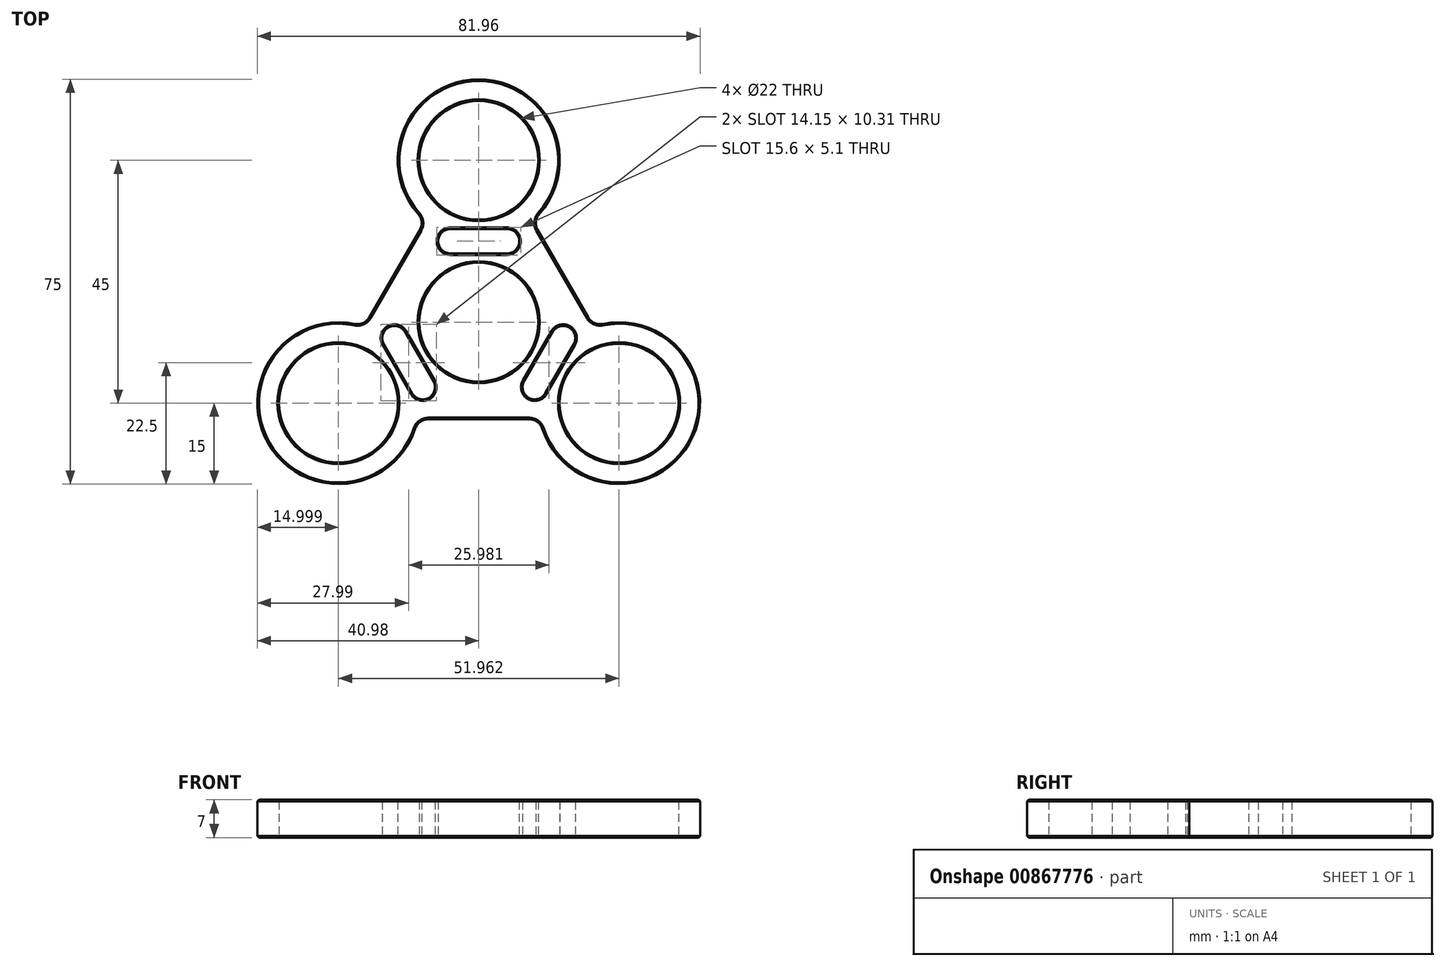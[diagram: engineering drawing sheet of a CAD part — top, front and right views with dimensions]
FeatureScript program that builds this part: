
annotation { "Feature Type Name" : "Feature", "Feature Type Description" : "" }
export const myFeature = defineFeature(function(context is Context, id is Id, definition is map)
    precondition{}
    {
        {
            var Q0;
            Q0=qCreatedBy(makeId("Top.planeOp"),FACE);
            var sketch = newSketch(context, id + "F0", { "sketchPlane" : qUnion([Q0])});
            skCircle(sketch, "E0", {"center": v(0, 0) * mm, "radius": 11 * mm});
            skCircle(sketch, "E1.cCircle", {"center": v(0, 0) * mm, "radius": 30 * mm, "construction": true});
            skLineSegment(sketch, "E1.0", {"start": v(0, 30) * mm, "end": v(25.98, -15) * mm, "construction": true});
            skLineSegment(sketch, "E1.1", {"start": v(25.98, -15) * mm, "end": v(-25.98, -15) * mm, "construction": true});
            skLineSegment(sketch, "E1.2", {"start": v(-25.98, -15) * mm, "end": v(0, 30) * mm, "construction": true});
            skCircle(sketch, "E2", {"center": v(0, 30) * mm, "radius": 11 * mm});
            skCircle(sketch, "E3.1.0", {"center": v(-25.98, -15) * mm, "radius": 11 * mm});
            skCircle(sketch, "E3.2.0", {"center": v(25.98, -15) * mm, "radius": 11 * mm});
            skArc(sketch, "E4", {"start": v(9.95, 18.77) * mm, "mid": v(0, 45) * mm, "end": v(-9.95, 18.77) * mm});
            skArc(sketch, "E5.1.0", {"start": v(-21.23, -0.77) * mm, "mid": v(-38.97, -22.5) * mm, "end": v(-11.28, -18) * mm});
            skArc(sketch, "E5.2.0", {"start": v(11.28, -18) * mm, "mid": v(38.97, -22.5) * mm, "end": v(21.23, -0.77) * mm});
            skLineSegment(sketch, "E6.2", {"start": v(11.28, -18) * mm, "end": v(-11.28, -18) * mm});
            skLineSegment(sketch, "E7.trimOffspring", {"start": v(-21.23, -0.77) * mm, "end": v(-9.95, 18.77) * mm});
            skLineSegment(sketch, "E8.trimOffspring", {"start": v(9.95, 18.77) * mm, "end": v(21.23, -0.77) * mm});
            skCircle(sketch, "E9", {"center": v(0, 0) * mm, "radius": 45 * mm, "construction": true});
            skSolve(sketch);
        }
        {
            var Q0;
            Q0=makeQuery(id+"F0.imprint","IMPRINT",FACE,{"disambiguationData":[TD([[makeQuery(id+"F0.imprint","IMPRINT",EDGE,{"derivedFrom":sQuery(id+"F0.wireOp",EDGE,"E0")}),-1.0]])]});
            extrude(context, id + "F1", {"entities" : qUnion([Q0]), "depth" : 7 * mm, "offsetDistance" : 25 * mm});
        }
        {
            var Q0;
            Q0=makeQuery(id+"F1.opExtrude","SWEPT_EDGE",EDGE,{"disambiguationData":[OSD([sQuery(id+"F0.wireOp",EDGE,"E5.2.0"),sQuery(id+"F0.wireOp",EDGE,"E6.2")])]});
            var Q1;
            Q1=makeQuery(id+"F1.opExtrude","SWEPT_EDGE",EDGE,{"disambiguationData":[OSD([sQuery(id+"F0.wireOp",EDGE,"E5.1.0"),sQuery(id+"F0.wireOp",EDGE,"E6.2")])]});
            var Q2;
            Q2=makeQuery(id+"F1.opExtrude","SWEPT_EDGE",EDGE,{"disambiguationData":[OSD([sQuery(id+"F0.wireOp",EDGE,"E5.1.0"),sQuery(id+"F0.wireOp",EDGE,"E7.trimOffspring")])]});
            var Q3;
            Q3=makeQuery(id+"F1.opExtrude","SWEPT_EDGE",EDGE,{"disambiguationData":[OSD([sQuery(id+"F0.wireOp",EDGE,"E4"),sQuery(id+"F0.wireOp",EDGE,"E8.trimOffspring")])]});
            var Q4;
            Q4=makeQuery(id+"F1.opExtrude","SWEPT_EDGE",EDGE,{"disambiguationData":[OSD([sQuery(id+"F0.wireOp",EDGE,"E5.2.0"),sQuery(id+"F0.wireOp",EDGE,"E8.trimOffspring")])]});
            var Q5;
            Q5=makeQuery(id+"F1.opExtrude","SWEPT_EDGE",EDGE,{"disambiguationData":[OSD([sQuery(id+"F0.wireOp",EDGE,"E4"),sQuery(id+"F0.wireOp",EDGE,"E7.trimOffspring")])]});
            fillet(context, id + "F2", {"entities" : qUnion([Q0, Q1, Q2, Q3, Q4, Q5]), "radius" : 2.5 * mm, "tangentPropagation" : true, "allowEdgeOverflow" : false});
        }
        {
            var Q0;
            Q0=makeQuery(id+"F1.opExtrude","CAP_FACE",FACE,{"disambiguationData":[OSD([sQuery(id+"F0.wireOp",EDGE,"E0"),sQuery(id+"F0.wireOp",EDGE,"E2"),sQuery(id+"F0.wireOp",EDGE,"E3.1.0"),sQuery(id+"F0.wireOp",EDGE,"E3.2.0"),sQuery(id+"F0.wireOp",EDGE,"E4"),sQuery(id+"F0.wireOp",EDGE,"E5.1.0"),sQuery(id+"F0.wireOp",EDGE,"E5.2.0"),sQuery(id+"F0.wireOp",EDGE,"E6.2"),sQuery(id+"F0.wireOp",EDGE,"E7.trimOffspring"),sQuery(id+"F0.wireOp",EDGE,"E8.trimOffspring")])],"isStart":true});
            var sketch = newSketch(context, id + "F3", { "sketchPlane" : qUnion([Q0])});
            skLineSegment(sketch, "E10.bottom", {"start": v(5.25, -12.75) * mm, "end": v(-5.25, -12.75) * mm});
            skLineSegment(sketch, "E10.top", {"start": v(5.25, -17.25) * mm, "end": v(-5.25, -17.25) * mm});
            skLineSegment(sketch, "E10.left", {"start": v(7.5, -15) * mm, "end": v(7.5, -15) * mm});
            skLineSegment(sketch, "E10.right", {"start": v(-7.5, -15) * mm, "end": v(-7.5, -15) * mm});
            skPoint(sketch, "E10.middle", {"position": v(0, -15) * mm});
            skPoint(sketch, "E11.center", {"position": v(0, 0) * mm});
            skPoint(sketch, "E12.visualSharp", {"position": v(7.5, -17.25) * mm});
            skArc(sketch, "E12.filletArc", {"start": v(5.25, -17.25) * mm, "mid": v(6.84, -16.6) * mm, "end": v(7.5, -15) * mm});
            skPoint(sketch, "E13.visualSharp", {"position": v(7.5, -12.75) * mm});
            skArc(sketch, "E13.filletArc", {"start": v(7.5, -15) * mm, "mid": v(6.84, -13.4) * mm, "end": v(5.25, -12.75) * mm});
            skPoint(sketch, "E14.visualSharp", {"position": v(-7.5, -17.25) * mm});
            skArc(sketch, "E14.filletArc", {"start": v(-7.5, -15) * mm, "mid": v(-6.84, -16.6) * mm, "end": v(-5.25, -17.25) * mm});
            skPoint(sketch, "E15.visualSharp", {"position": v(-7.5, -12.75) * mm});
            skArc(sketch, "E15.filletArc", {"start": v(-5.25, -12.75) * mm, "mid": v(-6.84, -13.4) * mm, "end": v(-7.5, -15) * mm});
            skPoint(sketch, "E16.1.0", {"position": v(13, 7.5) * mm});
            skArc(sketch, "E16.1.1", {"start": v(16.74, 1) * mm, "mid": v(17.79, 2.37) * mm, "end": v(17.56, 4.08) * mm});
            skPoint(sketch, "E16.1.2", {"position": v(14.8, -0.12) * mm});
            skLineSegment(sketch, "E16.1.3", {"start": v(12.31, 13.17) * mm, "end": v(17.56, 4.08) * mm});
            skArc(sketch, "E16.1.4", {"start": v(13.67, 1.83) * mm, "mid": v(15.03, 0.78) * mm, "end": v(16.74, 1) * mm});
            skPoint(sketch, "E16.1.5", {"position": v(11.19, 15.12) * mm});
            skPoint(sketch, "E16.1.6", {"position": v(7.3, 12.87) * mm});
            skPoint(sketch, "E16.1.7", {"position": v(18.69, 2.13) * mm});
            skLineSegment(sketch, "E16.1.8", {"start": v(8.42, 10.92) * mm, "end": v(13.67, 1.83) * mm});
            skArc(sketch, "E16.1.9", {"start": v(12.31, 13.17) * mm, "mid": v(10.95, 14.22) * mm, "end": v(9.24, 14) * mm});
            skArc(sketch, "E16.1.10", {"start": v(9.24, 14) * mm, "mid": v(8.2, 12.63) * mm, "end": v(8.42, 10.92) * mm});
            skPoint(sketch, "E16.2.0", {"position": v(-13, 7.5) * mm});
            skArc(sketch, "E16.2.1", {"start": v(-9.24, 14) * mm, "mid": v(-10.95, 14.22) * mm, "end": v(-12.31, 13.17) * mm});
            skPoint(sketch, "E16.2.2", {"position": v(-7.3, 12.87) * mm});
            skLineSegment(sketch, "E16.2.3", {"start": v(-17.56, 4.08) * mm, "end": v(-12.31, 13.17) * mm});
            skArc(sketch, "E16.2.4", {"start": v(-8.42, 10.92) * mm, "mid": v(-8.2, 12.63) * mm, "end": v(-9.24, 14) * mm});
            skPoint(sketch, "E16.2.5", {"position": v(-18.69, 2.13) * mm});
            skPoint(sketch, "E16.2.6", {"position": v(-14.8, -0.12) * mm});
            skPoint(sketch, "E16.2.7", {"position": v(-11.19, 15.12) * mm});
            skLineSegment(sketch, "E16.2.8", {"start": v(-13.67, 1.83) * mm, "end": v(-8.42, 10.92) * mm});
            skArc(sketch, "E16.2.9", {"start": v(-17.56, 4.08) * mm, "mid": v(-17.79, 2.37) * mm, "end": v(-16.74, 1) * mm});
            skArc(sketch, "E16.2.10", {"start": v(-16.74, 1) * mm, "mid": v(-15.03, 0.78) * mm, "end": v(-13.67, 1.83) * mm});
            skSolve(sketch);
        }
        {
            var Q0;
            Q0 = qSketchRegion(id + "F3", true);
            extrude(context, id + "F4", {"entities" : qUnion([Q0]), "operationType" : NewBodyOperationType.REMOVE, "oppositeDirection" : true, "depth" : 25 * mm, "offsetDistance" : 25 * mm});
        }
        {
            var Q0;
            Q0=makeQuery(id+"F1.opExtrude","CAP_FACE",FACE,{"disambiguationData":[OSD([sQuery(id+"F0.wireOp",EDGE,"E0"),sQuery(id+"F0.wireOp",EDGE,"E2"),sQuery(id+"F0.wireOp",EDGE,"E3.1.0"),sQuery(id+"F0.wireOp",EDGE,"E3.2.0"),sQuery(id+"F0.wireOp",EDGE,"E4"),sQuery(id+"F0.wireOp",EDGE,"E5.1.0"),sQuery(id+"F0.wireOp",EDGE,"E5.2.0"),sQuery(id+"F0.wireOp",EDGE,"E6.2"),sQuery(id+"F0.wireOp",EDGE,"E7.trimOffspring"),sQuery(id+"F0.wireOp",EDGE,"E8.trimOffspring")])],"isStart":true});
            var Q1;
            Q1=makeQuery(id+"F1.opExtrude","CAP_FACE",FACE,{"disambiguationData":[OSD([sQuery(id+"F0.wireOp",EDGE,"E0"),sQuery(id+"F0.wireOp",EDGE,"E2"),sQuery(id+"F0.wireOp",EDGE,"E3.1.0"),sQuery(id+"F0.wireOp",EDGE,"E3.2.0"),sQuery(id+"F0.wireOp",EDGE,"E4"),sQuery(id+"F0.wireOp",EDGE,"E5.1.0"),sQuery(id+"F0.wireOp",EDGE,"E5.2.0"),sQuery(id+"F0.wireOp",EDGE,"E6.2"),sQuery(id+"F0.wireOp",EDGE,"E7.trimOffspring"),sQuery(id+"F0.wireOp",EDGE,"E8.trimOffspring")])],"isStart":false});
            chamfer(context, id + "F5", {"entities" : qUnion([Q0, Q1]), "width" : .3 * mm, "tangentPropagation" : true});
        }
    });
